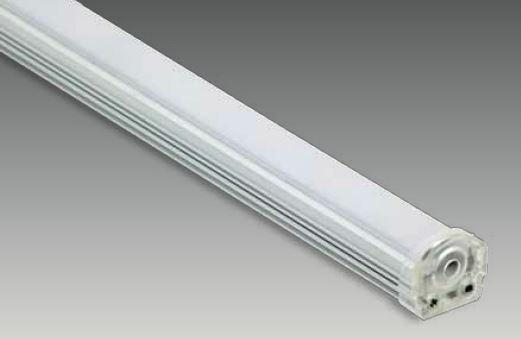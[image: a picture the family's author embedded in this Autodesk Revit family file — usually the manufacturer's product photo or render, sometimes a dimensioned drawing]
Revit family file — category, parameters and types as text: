
# Revit family: SD 0135 CVI
name_source: partatom
category: Lighting Fixtures
revit_build: Autodesk Revit 2017 (Build: 20160225_1515(x64)
units: mm (PartAtom-declared; Revit-internal decimal feet)

## family parameters
Cut with Voids When Loaded = No
Host = Face
Light Source = Yes
Part Type = Normal
Room Calculation Point = No
Round Connector Dimension = Use Diameter
Shared = No

## types (2) — shared parameters
Apparent Load = 2 VA
Color Filter = 16777215
Default Elevation = 1219 mm
Dimming Lamp Color Temperature Shift = <None>
Emit Shape Visible in Rendering = Yes
Emit from Rectangle Length = 15 mm  [stored 0.0492126 ft]
Emit from Rectangle Width = 130 mm  [stored 0.426509 ft]
Light Source Symbol Size = 610 mm
Manufacturer = ARLIGHT
Type Image = SD 0135 CVI.JPG
Wattage Comments = 2

## type names (no varying parameters)
- SDCVI.135.2.30
- SDCVI.135.2.40

note: [stored X ft] marks values corroborated as IEEE doubles in the binary element streams (Revit-internal decimal feet)

## geometry (parser evidence)
native form markers: Sweep x3
no freeform markers — native parametric forms only
